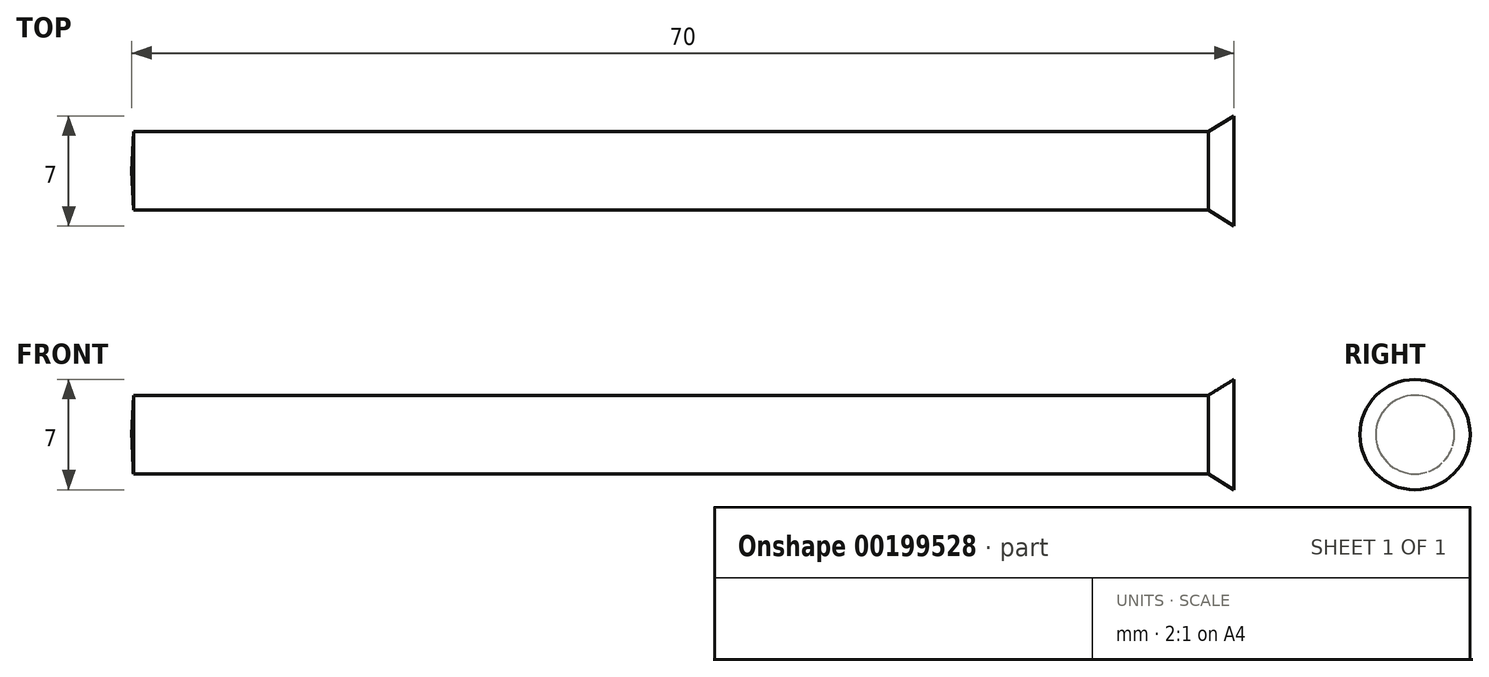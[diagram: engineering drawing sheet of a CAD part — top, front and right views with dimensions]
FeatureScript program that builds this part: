
annotation { "Feature Type Name" : "Feature", "Feature Type Description" : "" }
export const myFeature = defineFeature(function(context is Context, id is Id, definition is map)
    precondition{}
    {
        {
            var Q0;
            Q0=qCreatedBy(makeId("Front.planeOp"),FACE);
            var sketch = newSketch(context, id + "F0", { "sketchPlane" : qUnion([Q0])});
            skLineSegment(sketch, "E0", {"start": v(-39.53, 0) * mm, "end": v(30.47, 0) * mm});
            skLineSegment(sketch, "E1", {"start": v(30.47, 0) * mm, "end": v(30.47, -3.5) * mm});
            skLineSegment(sketch, "E2", {"start": v(30.47, -3.5) * mm, "end": v(28.84, -2.5) * mm});
            skLineSegment(sketch, "E3", {"start": v(28.84, -2.5) * mm, "end": v(-39.43, -2.5) * mm});
            skLineSegment(sketch, "E4", {"start": v(-39.43, -2.5) * mm, "end": v(-39.53, 0) * mm});
            skSolve(sketch);
        }
        {
            var Q0;
            Q0=makeQuery(id+"F0.imprint","IMPRINT",FACE,{"disambiguationData":[TD([[makeQuery(id+"F0.imprint","IMPRINT",EDGE,{"derivedFrom":sQuery(id+"F0.wireOp",EDGE,"E0")}),-1.0]])]});
            var Q1;
            Q1=sQuery(id+"F0.wireOp",EDGE,"E0");
            revolve(context, id + "F1", {"entities" : qUnion([Q0]), "axis" : qUnion([Q1]), "revolveType" : RevolveType.FULL});
        }
    });
